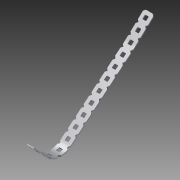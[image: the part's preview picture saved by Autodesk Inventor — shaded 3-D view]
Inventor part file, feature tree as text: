
AUTODESK INVENTOR PART (.ipt)
format: ipt  version: 2014 SP1 (Build 180222100, 222)  size: 1,006,592 bytes
history: native  units: in
note: dims shown in document units (in); Inventor stores cm internally (conversion verified against a paired STEP export)
features: other x3, sketch x3, imported_body x1, extrude x1
ambient origin geometry x8: Origin, YZ Plane, XZ Plane, XY Plane, X Axis, Y Axis, Z Axis, Center Point
bodies: Body1 (feature_tree)
feature tree (8):
  parser-record x1  (decoder bookkeeping rows leaked as tree rows — omitted from the tree; the rows remain in map.json)
  imported_body  "Base1"
  extrude  "Extrusion1"  Depth=1.0in TaperAngle=0.0deg
  other  "Bend Part1"
  other  "Bend Part2"
  sketch  "Sketch1"  dims[d0=7.5in d1=1.0in d2=0.0in]
  sketch  "Sketch3"  dims[d3=0.8in d4=0.5944in]
  sketch  "Sketch4"  dims[d5=1.0in d6=0.024in]
